# Revit family: Ballorex Dynamic
name_source: partatom
category: Арматура трубопроводов
revit_build: Autodesk Revit 2017 (Build: 20171027_0315(x64)
units: mm (PartAtom-declared; Revit-internal decimal feet)

## family parameters
Всегда вертикально = Да
На основе рабочей плоскости = Нет
Общий = Нет
При загрузке вырезать с полостями = Нет
Размер круглого соединителя = Использовать радиус
Тип детали = Вставляется

## types (10) — shared parameters
ADSK_Единица измерения = шт
ADSK_Завод-изготовитель = Meibes
ADSK_Наименование = Клапан балансировчный Ballorex Dynamic
URL = www.meibes.ru/
Группа модели = Клапан балансировчный Ballorex Dynamic
Изготовитель = Meibes
Материал полимера = Фильтр_Черный
Материал стальной части = Фильтр_Латунь
Материал фитинга = РВК_Полипропилен PPR
Разработчик = ООО ПРОРУБИМ
Разработчик (телефон) = +7(495)649-85-43
Разработчик модели (URL) = http://prorubim.com
zero-valued in all types: ADSK_Масса

## per-type parameters (varying)
| type | ADSK_Код изделия | ADSK_Обозначение | B | B/2 | D2 | D3 | DN | DN+t | H1 | H2 | L | L1 | L2 | R | l2 | t | x |
| 25S | ME 80597.006 | DN 25S | 71 мм | 36 мм | 17 мм | 40 мм | 25 мм | 30 мм | 81 мм | 56 мм | 127 мм | 55 мм | 35 мм | 13 мм | 68 мм | 5 мм | 106 мм |
| 20S | ME 80597.004 | DN 20S | 55 мм | 28 мм | 14 мм | 29 мм | 20 мм | 23 мм | 83 мм | 49 мм | 120 мм | 50 мм | 35 мм | 10 мм | 68 мм | 3 мм | 100 мм |
| 15L | ME 80597.001 | DN 15L | 44 мм | 22 мм | 12 мм | 30 мм | 15 мм | 20 мм | 76 мм | 35 мм | 95 мм | 35 мм | 15 мм | 8 мм | 68 мм | 5 мм | 79 мм |
| 32H | ME 80597.008 | DN 32H | 82 мм | 41 мм | 21 мм | 47 мм | 32 мм | 37 мм | 87 мм | 72 мм | 154 мм | 65 мм | 35 мм | 16 мм | 68 мм | 5 мм | 128 мм |
| 40H | ME 80597.010 | DN 40H | 110 мм | 55 мм | 25 мм | 55 мм | 40 мм | 45 мм | 212 мм | 72 мм | 189 мм | 120 мм | 100 мм | 20 мм | 75 мм | 5 мм | 158 мм |
| 50H | ME 80597.013 | DN 50H | 111 мм | 55 мм | 30 мм | 65 мм | 50 мм | 55 мм | 210 мм | 72 мм | 195 мм | 120 мм | 100 мм | 25 мм | 75 мм | 5 мм | 163 мм |
| 15H | ME 80597.003 | DN 15H | 44 мм | 22 мм | 12 мм | 30 мм | 15 мм | 20 мм | 76 мм | 35 мм | 95 мм | 35 мм | 15 мм | 8 мм | 68 мм | 5 мм | 79 мм |
| 15S | ME 80597.002 | DN 15S | 44 мм | 22 мм | 12 мм | 30 мм | 15 мм | 20 мм | 76 мм | 35 мм | 95 мм | 35 мм | 15 мм | 8 мм | 68 мм | 5 мм | 79 мм |
| 20H | ME 80597.005 | DN 20H | 55 мм | 28 мм | 14 мм | 29 мм | 20 мм | 23 мм | 83 мм | 49 мм | 120 мм | 50 мм | 35 мм | 10 мм | 68 мм | 3 мм | 100 мм |
| 25H | ME 80597.007 | DN 25H | 71 мм | 36 мм | 17 мм | 40 мм | 25 мм | 30 мм | 81 мм | 56 мм | 127 мм | 55 мм | 35 мм | 13 мм | 68 мм | 5 мм | 106 мм |
